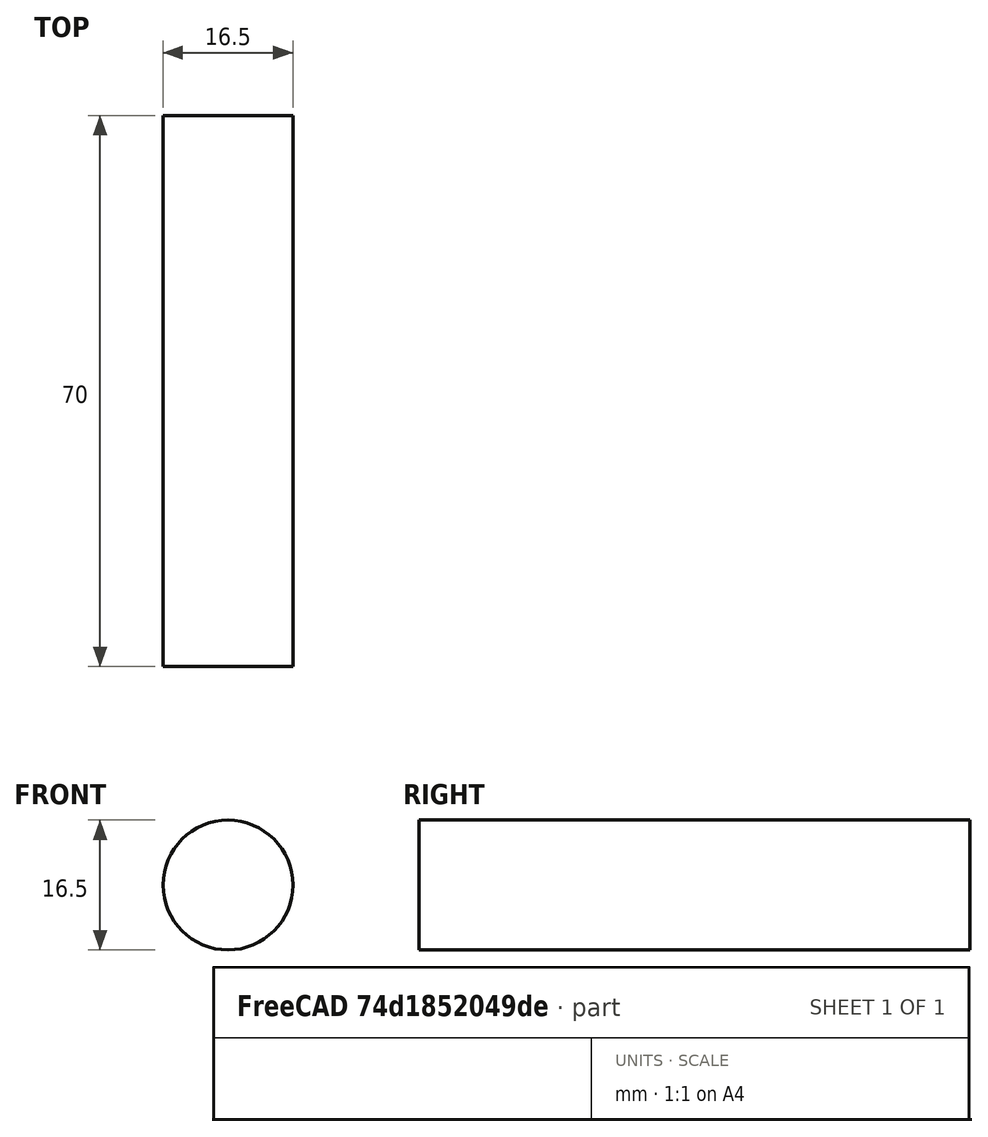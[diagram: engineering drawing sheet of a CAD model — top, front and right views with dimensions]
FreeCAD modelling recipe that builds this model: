
FCSTD DOCUMENT  (FreeCAD 1.0R39285 (Git))
Label: wire
License: All rights reserved
LicenseURL: https://en.wikipedia.org/wiki/All_rights_reserved
objects: Sketcher::SketchObject×1, PartDesign::Pad×1, PartDesign::Body×1
note: 6 computed .brp shape members not serialized (recipe doc carries the construction recipe); baked Part::Feature solids carry a one-line shape summary decoded from their .brp

FEATURE [Sketcher::SketchObject] Sketch
  ArcFitTolerance = 1e-06
  AttachmentSupport = -> [XZ_Plane]
  FullyConstrained = true
  MakeInternals = false
  MapMode = 5
  Placement = pos=(0,0,0) rot=(1,0,0;1.5708rad)
  sketch-geometry (1):
    g0: Circle CenterX=0 CenterY=0 CenterZ=0 NormalX=0 NormalY=0 NormalZ=1 AngleXU=0 Radius=8.25
  constraints (2):
    c: Coincident(g0,g-1)
    c: Diameter(g0) = 16.5
FEATURE [PartDesign::Pad] Pad
  Direction = (0,-1,2e-16)
  Length = 70
  Length2 = 10
  Placement = pos=(0,0,0) rot=(1,0,0;1.5708rad)
  Profile = -> Sketch
  ReferenceAxis = -> Sketch [N_Axis]
  Refine = true
  Suppressed = false
  Type = 0
FEATURE [PartDesign::Body] Body
  AllowCompound = false
  Group = -> [Sketch,Pad]
  Origin = -> Origin
  Tip = -> Pad
